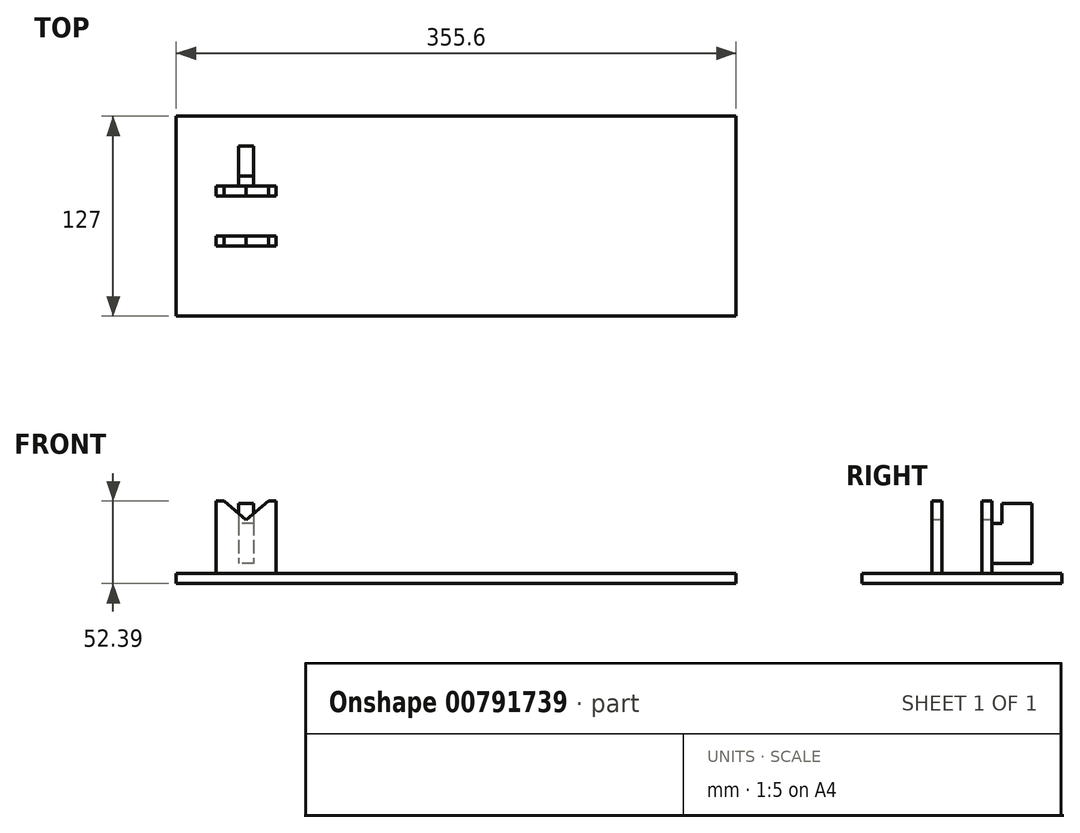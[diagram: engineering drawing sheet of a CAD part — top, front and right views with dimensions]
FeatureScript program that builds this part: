
annotation { "Feature Type Name" : "Feature", "Feature Type Description" : "" }
export const myFeature = defineFeature(function(context is Context, id is Id, definition is map)
    precondition{}
    {
        {
            var Q0;
            Q0=qCreatedBy(makeId("Top.planeOp"),FACE);
            var sketch = newSketch(context, id + "F0", { "sketchPlane" : qUnion([Q0])});
            skLineSegment(sketch, "E0.bottom", {"start": v(0, 4.6) * mm, "end": v(355.6, 4.6) * mm});
            skLineSegment(sketch, "E0.top", {"start": v(0, 131.6) * mm, "end": v(355.6, 131.6) * mm});
            skLineSegment(sketch, "E0.left", {"start": v(0, 4.6) * mm, "end": v(0, 131.6) * mm});
            skLineSegment(sketch, "E0.right", {"start": v(355.6, 4.6) * mm, "end": v(355.6, 131.6) * mm});
            skSolve(sketch);
        }
        {
            var Q0;
            Q0=qSketchRegion(id+"F0",true);
            extrude(context, id + "F1", {"entities" : qUnion([Q0]), "depth" : 6.35 * mm, "offsetDistance" : 25.4 * mm});
        }
        {
            var Q0;
            Q0=makeQuery(id+"F1.opExtrude","CAP_FACE",FACE,{"disambiguationData":[OSD([sQuery(id+"F0.wireOp",EDGE,"E0.bottom"),sQuery(id+"F0.wireOp",EDGE,"E0.top"),sQuery(id+"F0.wireOp",EDGE,"E0.left"),sQuery(id+"F0.wireOp",EDGE,"E0.right")])],"isStart":false});
            var sketch = newSketch(context, id + "F2", { "sketchPlane" : qUnion([Q0])});
            skLineSegment(sketch, "E1.bottom", {"start": v(25.4, 49.04) * mm, "end": v(63.5, 49.04) * mm});
            skLineSegment(sketch, "E1.top", {"start": v(25.4, 55.4) * mm, "end": v(63.5, 55.4) * mm});
            skLineSegment(sketch, "E1.left", {"start": v(25.4, 49.04) * mm, "end": v(25.4, 55.4) * mm});
            skLineSegment(sketch, "E1.right", {"start": v(63.5, 49.04) * mm, "end": v(63.5, 55.4) * mm});
            skLineSegment(sketch, "E2.0.1.0", {"start": v(25.4, 80.8) * mm, "end": v(63.5, 80.8) * mm});
            skLineSegment(sketch, "E2.0.1.1", {"start": v(25.4, 87.14) * mm, "end": v(63.5, 87.14) * mm});
            skLineSegment(sketch, "E2.0.1.2", {"start": v(63.5, 80.8) * mm, "end": v(63.5, 87.14) * mm});
            skLineSegment(sketch, "E2.0.1.3", {"start": v(25.4, 80.8) * mm, "end": v(25.4, 87.14) * mm});
            skLineSegment(sketch, "E2.direction1", {"start": v(25.4, 49.04) * mm, "end": v(50.8, 49.04) * mm, "construction": true});
            skLineSegment(sketch, "E2.direction2", {"start": v(25.4, 49.04) * mm, "end": v(25.4, 80.8) * mm, "construction": true});
            skSolve(sketch);
        }
        {
            var Q0;
            Q0=qSketchRegion(id+"F2",true);
            extrude(context, id + "F3", {"entities" : qUnion([Q0]), "operationType" : NewBodyOperationType.ADD, "depth" : 50.8 * mm, "offsetDistance" : 25.4 * mm});
        }
        {
            var Q0;
            Q0=makeQuery(id+"F3.opExtrude","SWEPT_FACE",FACE,{"disambiguationData":[OSD([sQuery(id+"F2.wireOp",EDGE,"E1.bottom")])]});
            var sketch = newSketch(context, id + "F4", { "sketchPlane" : qUnion([Q0])});
            skCircle(sketch, "E3", {"center": v(44.45, 57.15) * mm, "radius": 12.7 * mm, "construction": true});
            skLineSegment(sketch, "E4", {"start": v(25.4, 57.15) * mm, "end": v(63.5, 57.15) * mm});
            skLineSegment(sketch, "E5.0", {"start": v(25.4, 52.39) * mm, "end": v(30.37, 52.39) * mm});
            skLineSegment(sketch, "E6", {"start": v(25.4, 57.15) * mm, "end": v(25.4, 52.39) * mm});
            skLineSegment(sketch, "E7", {"start": v(63.5, 57.15) * mm, "end": v(63.5, 52.39) * mm});
            skLineSegment(sketch, "E8.trimOffspring", {"start": v(58.53, 52.39) * mm, "end": v(63.5, 52.39) * mm});
            skPoint(sketch, "E9.orphan", {"position": v(44.45, 39.19) * mm});
            skLineSegment(sketch, "E10.0", {"start": v(30.37, 52.39) * mm, "end": v(44.45, 40.57) * mm});
            skLineSegment(sketch, "E11.0", {"start": v(58.53, 52.39) * mm, "end": v(44.45, 40.57) * mm});
            skLineSegment(sketch, "E12", {"start": v(36.29, 47.42) * mm, "end": v(44.45, 57.15) * mm, "construction": true});
            skLineSegment(sketch, "E13", {"start": v(52.61, 47.42) * mm, "end": v(44.45, 57.15) * mm, "construction": true});
            skSolve(sketch);
        }
        {
            var Q0;
            Q0=qSketchRegion(id+"F4",true);
            var Q1;
            Q1=makeQuery(id+"F3.opExtrude","SWEPT_FACE",FACE,{"disambiguationData":[OSD([sQuery(id+"F2.wireOp",EDGE,"E2.0.1.1")])]});
            extrude(context, id + "F5", {"entities" : qUnion([Q0, Q1]), "operationType" : NewBodyOperationType.REMOVE, "oppositeDirection" : true, "depth" : 50.8 * mm, "offsetDistance" : 25.4 * mm});
        }
        {
            var Q0;
            Q0=makeQuery(id+"F3.opExtrude","SWEPT_FACE",FACE,{"disambiguationData":[OSD([sQuery(id+"F2.wireOp",EDGE,"E2.0.1.1")])]});
            var sketch = newSketch(context, id + "F6", { "sketchPlane" : qUnion([Q0])});
            skLineSegment(sketch, "E14.bottom", {"start": v(-49.21, 38.1) * mm, "end": v(-39.69, 38.1) * mm});
            skLineSegment(sketch, "E14.top", {"start": v(-49.21, 12.7) * mm, "end": v(-39.69, 12.7) * mm});
            skLineSegment(sketch, "E14.left", {"start": v(-49.21, 38.1) * mm, "end": v(-49.21, 12.7) * mm});
            skLineSegment(sketch, "E14.right", {"start": v(-39.69, 38.1) * mm, "end": v(-39.69, 12.7) * mm});
            skSolve(sketch);
        }
        {
            var Q0;
            Q0=qSketchRegion(id+"F6",true);
            extrude(context, id + "F7", {"entities" : qUnion([Q0]), "operationType" : NewBodyOperationType.ADD, "depth" : 25.4 * mm, "offsetDistance" : 25.4 * mm});
        }
        {
            var Q0;
            Q0=makeQuery(id+"F7.opExtrude","SWEPT_FACE",FACE,{"disambiguationData":[OSD([sQuery(id+"F6.wireOp",EDGE,"E14.bottom")])]});
            var sketch = newSketch(context, id + "F8", { "sketchPlane" : qUnion([Q0])});
            skLineSegment(sketch, "E15.bottom", {"start": v(49.21, 112.54) * mm, "end": v(39.69, 112.54) * mm});
            skLineSegment(sketch, "E15.top", {"start": v(49.21, 93.5) * mm, "end": v(39.69, 93.5) * mm});
            skLineSegment(sketch, "E15.left", {"start": v(49.21, 112.54) * mm, "end": v(49.21, 93.5) * mm});
            skLineSegment(sketch, "E15.right", {"start": v(39.69, 112.54) * mm, "end": v(39.69, 93.5) * mm});
            skSolve(sketch);
        }
        {
            var Q0;
            Q0=qSketchRegion(id+"F8",true);
            extrude(context, id + "F9", {"entities" : qUnion([Q0]), "operationType" : NewBodyOperationType.ADD, "depth" : 12.7 * mm, "offsetDistance" : 25.4 * mm});
        }
    });
